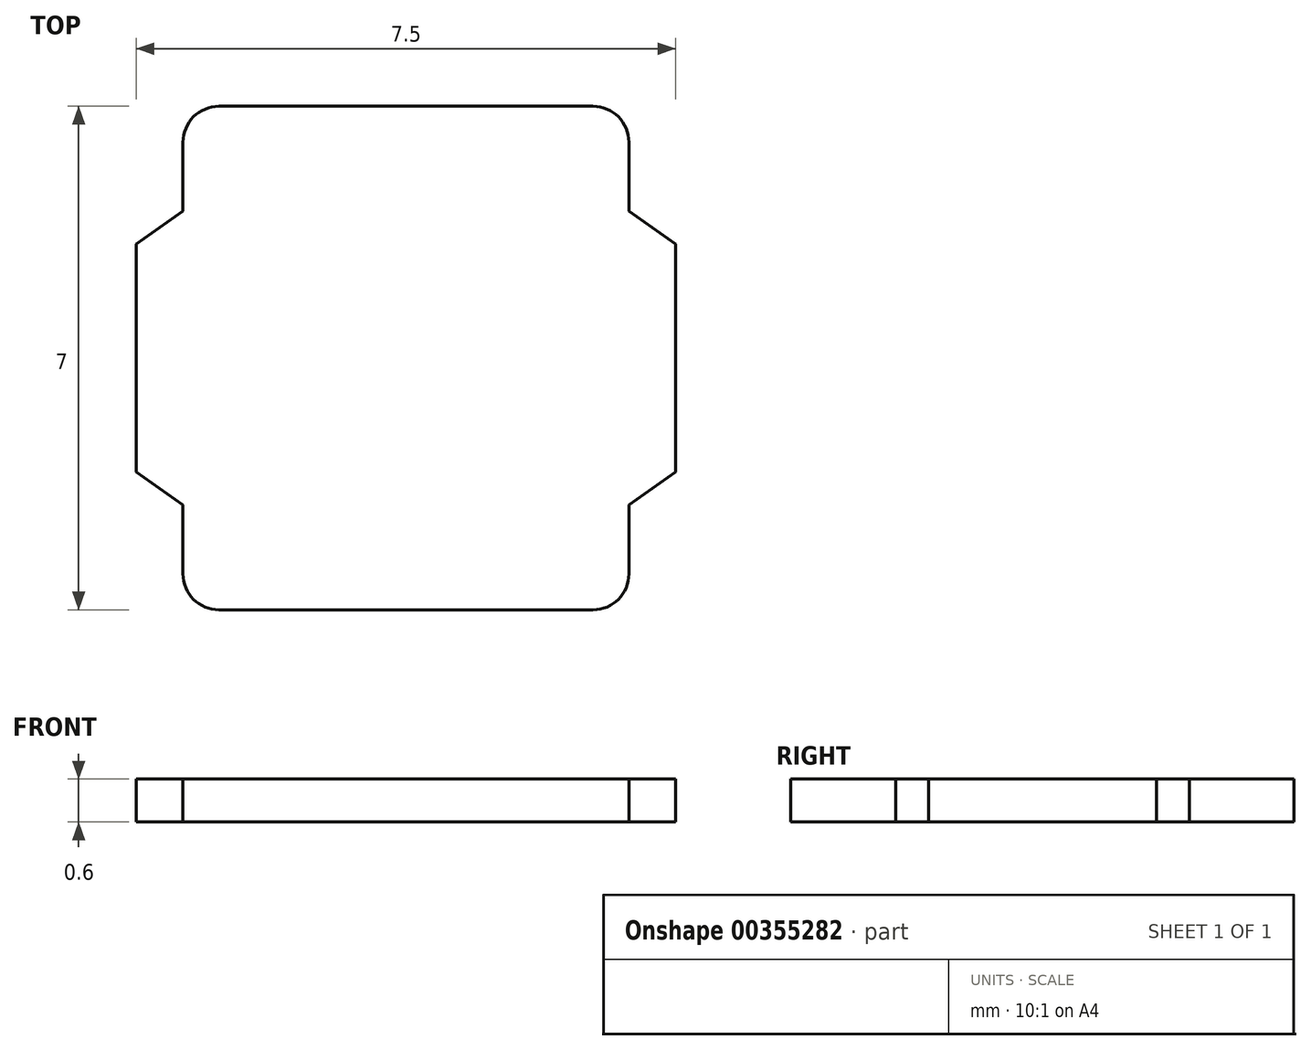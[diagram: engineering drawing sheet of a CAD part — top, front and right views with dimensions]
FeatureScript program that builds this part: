
annotation { "Feature Type Name" : "Feature", "Feature Type Description" : "" }
export const myFeature = defineFeature(function(context is Context, id is Id, definition is map)
    precondition{}
    {
        {
            var Q0;
            Q0=qCreatedBy(makeId("Top.planeOp"),FACE);
            var sketch = newSketch(context, id + "F0", { "sketchPlane" : qUnion([Q0])});
            skLineSegment(sketch, "E0.bottom", {"start": v(3.1, 3.5) * mm, "end": v(-3.1, 3.5) * mm});
            skLineSegment(sketch, "E0.top", {"start": v(3.1, -3.5) * mm, "end": v(-3.1, -3.5) * mm});
            skLineSegment(sketch, "E0.left", {"start": v(3.1, 3.5) * mm, "end": v(3.1, -3.5) * mm});
            skLineSegment(sketch, "E0.right", {"start": v(-3.1, 3.5) * mm, "end": v(-3.1, -3.5) * mm});
            skPoint(sketch, "E0.middle", {"position": v(0, 0) * mm});
            skSolve(sketch);
        }
        {
            var Q0;
            Q0=qCreatedBy(makeId("Top.planeOp"),FACE);
            var sketch = newSketch(context, id + "F1", { "sketchPlane" : qUnion([Q0])});
            skLineSegment(sketch, "E1", {"start": v(0, 3.5) * mm, "end": v(-1.03, 3.5) * mm});
            skLineSegment(sketch, "E2", {"start": v(-1.03, 3.5) * mm, "end": v(-3.75, 1.59) * mm});
            skLineSegment(sketch, "E3", {"start": v(-3.75, 1.59) * mm, "end": v(-3.75, 0) * mm});
            skLineSegment(sketch, "E4", {"start": v(0, 2.46) * mm, "end": v(0, -1.99) * mm, "construction": true});
            skLineSegment(sketch, "E5", {"start": v(2.4, 0) * mm, "end": v(-2.05, 0) * mm, "construction": true});
            skLineSegment(sketch, "E6.MirrorCS", {"start": v(3.75, 1.59) * mm, "end": v(3.75, 0) * mm});
            skLineSegment(sketch, "E7.MirrorCS", {"start": v(1.03, 3.5) * mm, "end": v(3.75, 1.59) * mm});
            skLineSegment(sketch, "E8.MirrorCS", {"start": v(0, 3.5) * mm, "end": v(1.03, 3.5) * mm});
            skLineSegment(sketch, "E9.MirrorCS", {"start": v(-3.75, -1.59) * mm, "end": v(-3.75, 0) * mm});
            skLineSegment(sketch, "E10.MirrorCS", {"start": v(3.75, -1.59) * mm, "end": v(3.75, 0) * mm});
            skLineSegment(sketch, "E11.MirrorCS", {"start": v(0, -3.5) * mm, "end": v(-1.03, -3.5) * mm});
            skLineSegment(sketch, "E12.MirrorCS", {"start": v(0, -3.5) * mm, "end": v(1.03, -3.5) * mm});
            skLineSegment(sketch, "E13.MirrorCS", {"start": v(-1.03, -3.5) * mm, "end": v(-3.75, -1.59) * mm});
            skLineSegment(sketch, "E14.MirrorCS", {"start": v(1.03, -3.5) * mm, "end": v(3.75, -1.59) * mm});
            skSolve(sketch);
        }
        {
            var Q0;
            Q0=qSketchRegion(id+"F1",true);
            var Q1;
            Q1=qSketchRegion(id+"F0",true);
            extrude(context, id + "F2", {"entities" : qUnion([Q0, Q1]), "depth" : 0.6 * mm});
        }
        {
            var Q0;
            Q0=makeQuery(id+"F2.opExtrude","SWEPT_BODY",BODY,{"disambiguationData":[OSD([sQuery(id+"F0.wireOp",EDGE,"E0.bottom"),sQuery(id+"F0.wireOp",EDGE,"E0.top"),sQuery(id+"F0.wireOp",EDGE,"E0.left"),sQuery(id+"F0.wireOp",EDGE,"E0.right")])]});
            var Q1;
            Q1=makeQuery(id+"F2.opExtrude","SWEPT_BODY",BODY,{"disambiguationData":[OSD([sQuery(id+"F1.wireOp",EDGE,"E1"),sQuery(id+"F1.wireOp",EDGE,"E2"),sQuery(id+"F1.wireOp",EDGE,"E3"),sQuery(id+"F1.wireOp",EDGE,"E6.MirrorCS"),sQuery(id+"F1.wireOp",EDGE,"E7.MirrorCS"),sQuery(id+"F1.wireOp",EDGE,"E8.MirrorCS"),sQuery(id+"F1.wireOp",EDGE,"E9.MirrorCS"),sQuery(id+"F1.wireOp",EDGE,"E10.MirrorCS"),sQuery(id+"F1.wireOp",EDGE,"E11.MirrorCS"),sQuery(id+"F1.wireOp",EDGE,"E12.MirrorCS"),sQuery(id+"F1.wireOp",EDGE,"E13.MirrorCS"),sQuery(id+"F1.wireOp",EDGE,"E14.MirrorCS")])]});
            booleanBodies(context, id + "F3", {"operationType" : BooleanOperationType.UNION, "tools" : qUnion([Q0, Q1])});
        }
        {
            var Q0;
            Q0=makeQuery(id+"F2.opExtrude","SWEPT_EDGE",EDGE,{"disambiguationData":[OSD([sQuery(id+"F0.wireOp",EDGE,"E0.bottom"),sQuery(id+"F0.wireOp",EDGE,"E0.right")])]});
            var Q1;
            Q1=makeQuery(id+"F2.opExtrude","SWEPT_EDGE",EDGE,{"disambiguationData":[OSD([sQuery(id+"F0.wireOp",EDGE,"E0.top"),sQuery(id+"F0.wireOp",EDGE,"E0.right")])]});
            var Q2;
            Q2=makeQuery(id+"F2.opExtrude","SWEPT_EDGE",EDGE,{"disambiguationData":[OSD([sQuery(id+"F0.wireOp",EDGE,"E0.top"),sQuery(id+"F0.wireOp",EDGE,"E0.left")])]});
            var Q3;
            Q3=makeQuery(id+"F2.opExtrude","SWEPT_EDGE",EDGE,{"disambiguationData":[OSD([sQuery(id+"F0.wireOp",EDGE,"E0.bottom"),sQuery(id+"F0.wireOp",EDGE,"E0.left")])]});
            fillet(context, id + "F4", {"entities" : qUnion([Q0, Q1, Q2, Q3]), "radius" : 0.5 * mm, "tangentPropagation" : true, "allowEdgeOverflow" : false});
        }
    });
